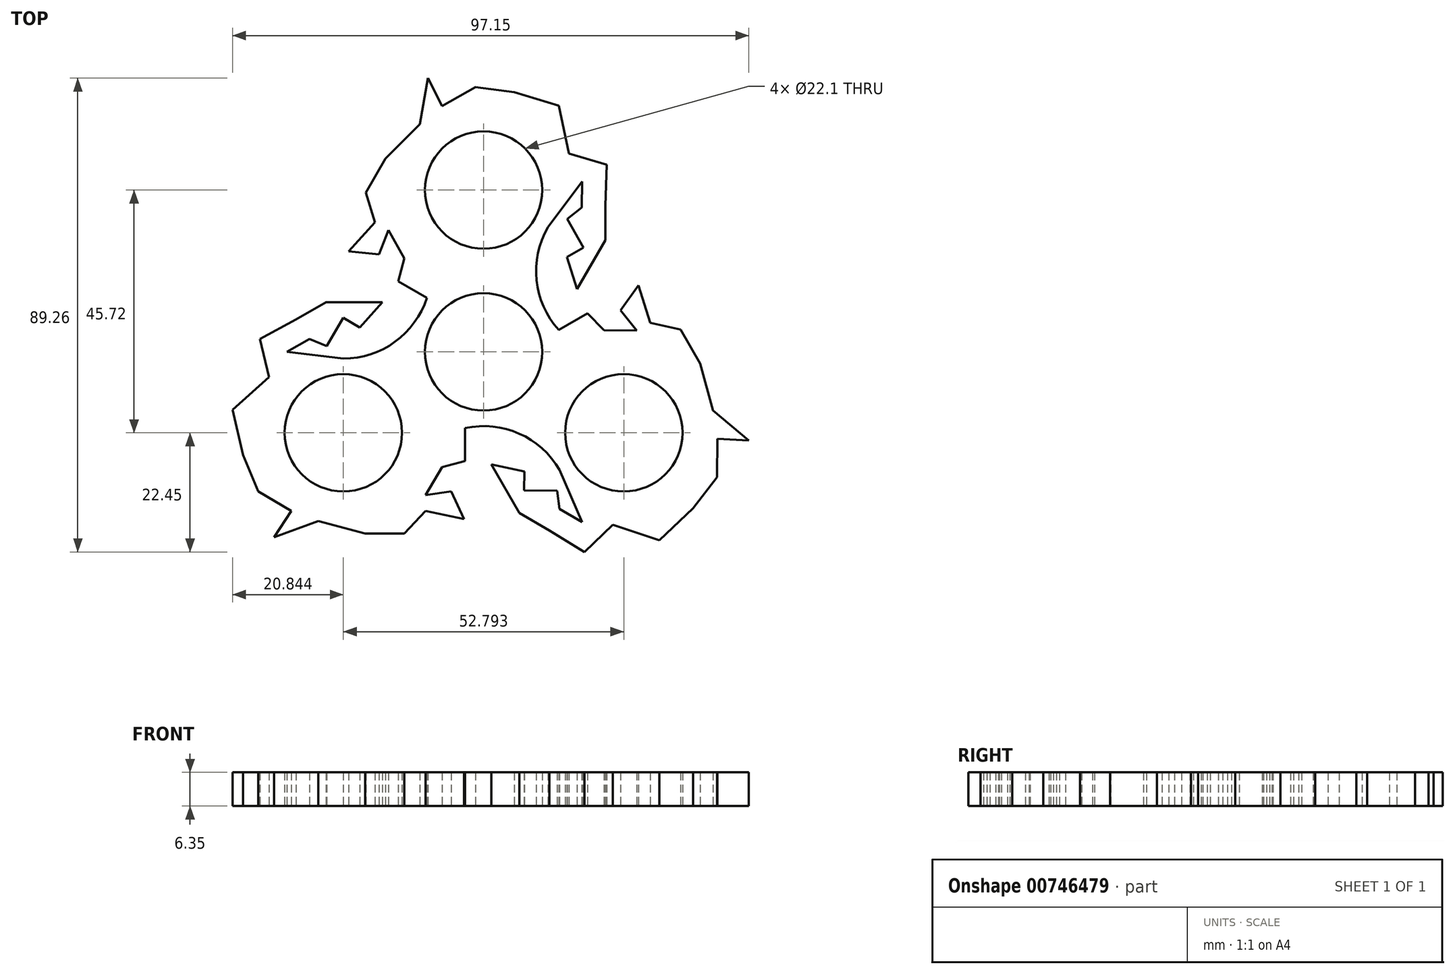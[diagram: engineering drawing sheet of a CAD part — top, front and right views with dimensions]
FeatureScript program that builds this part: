
annotation { "Feature Type Name" : "Feature", "Feature Type Description" : "" }
export const myFeature = defineFeature(function(context is Context, id is Id, definition is map)
    precondition{}
    {
        {
            var Q0;
            Q0=qCreatedBy(makeId("Top.planeOp"),FACE);
            var sketch = newSketch(context, id + "F0", { "sketchPlane" : qUnion([Q0])});
            skCircle(sketch, "E0", {"center": v(0, 0) * mm, "radius": 11.05 * mm});
            skCircle(sketch, "E1", {"center": v(0, 0) * mm, "radius": 13.97 * mm});
            skCircle(sketch, "E2", {"center": v(0, 30.48) * mm, "radius": 11.05 * mm});
            skCircle(sketch, "E3", {"center": v(0, 30.48) * mm, "radius": 13.97 * mm});
            skCircle(sketch, "E4.1.0", {"center": v(-26.4, -15.24) * mm, "radius": 13.97 * mm});
            skCircle(sketch, "E4.1.1", {"center": v(-26.4, -15.24) * mm, "radius": 11.05 * mm});
            skCircle(sketch, "E4.2.0", {"center": v(26.4, -15.24) * mm, "radius": 13.97 * mm});
            skCircle(sketch, "E4.2.1", {"center": v(26.4, -15.24) * mm, "radius": 11.05 * mm});
            skArc(sketch, "E5", {"start": v(-26.4, -1.27) * mm, "mid": v(-12.1, 6.99) * mm, "end": v(-12.1, 23.5) * mm});
            skArc(sketch, "E6.1.0", {"start": v(14.3, -22.22) * mm, "mid": v(0, -13.97) * mm, "end": v(-14.3, -22.23) * mm});
            skArc(sketch, "E6.2.0", {"start": v(12.1, 23.5) * mm, "mid": v(12.1, 6.99) * mm, "end": v(26.4, -1.27) * mm});
            skLineSegment(sketch, "E7", {"start": v(-37.03, 0) * mm, "end": v(-32.77, 2.41) * mm});
            skLineSegment(sketch, "E8", {"start": v(-32.77, 2.41) * mm, "end": v(-29.55, 1.1) * mm});
            skLineSegment(sketch, "E9", {"start": v(-29.55, 1.1) * mm, "end": v(-26.4, 6.44) * mm});
            skLineSegment(sketch, "E10", {"start": v(-26.4, 6.44) * mm, "end": v(-23.32, 4.62) * mm});
            skLineSegment(sketch, "E11", {"start": v(-23.32, 4.62) * mm, "end": v(-19.05, 9.33) * mm});
            skLineSegment(sketch, "E12", {"start": v(-19.05, 9.33) * mm, "end": v(-23.12, 9.33) * mm});
            skLineSegment(sketch, "E13", {"start": v(-23.12, 9.33) * mm, "end": v(-29.65, 9.33) * mm});
            skLineSegment(sketch, "E14", {"start": v(-29.65, 9.33) * mm, "end": v(-35.32, 6.1) * mm});
            skLineSegment(sketch, "E15", {"start": v(-35.32, 6.1) * mm, "end": v(-42.13, 2.41) * mm});
            skLineSegment(sketch, "E16", {"start": v(-42.13, 2.41) * mm, "end": v(-40.37, -4.74) * mm});
            skLineSegment(sketch, "E17", {"start": v(-40.37, -4.74) * mm, "end": v(-47.24, -10.92) * mm});
            skLineSegment(sketch, "E18", {"start": v(-47.24, -10.92) * mm, "end": v(-45.25, -19.44) * mm});
            skLineSegment(sketch, "E19", {"start": v(-45.25, -19.44) * mm, "end": v(-42.42, -26.24) * mm});
            skLineSegment(sketch, "E20", {"start": v(-42.42, -26.24) * mm, "end": v(-36.17, -29.93) * mm});
            skLineSegment(sketch, "E21", {"start": v(-36.17, -29.93) * mm, "end": v(-39.4, -34.88) * mm});
            skLineSegment(sketch, "E22", {"start": v(-39.4, -34.88) * mm, "end": v(-31.15, -31.86) * mm});
            skLineSegment(sketch, "E23", {"start": v(-31.15, -31.86) * mm, "end": v(-22.27, -34.19) * mm});
            skLineSegment(sketch, "E24", {"start": v(-22.27, -34.19) * mm, "end": v(-14.9, -34.19) * mm});
            skLineSegment(sketch, "E25", {"start": v(-14.9, -34.19) * mm, "end": v(-10.92, -29.93) * mm});
            skLineSegment(sketch, "E26", {"start": v(-10.92, -29.93) * mm, "end": v(-3.71, -31.5) * mm});
            skLineSegment(sketch, "E27", {"start": v(-3.71, -31.5) * mm, "end": v(-6.1, -26.24) * mm});
            skLineSegment(sketch, "E28", {"start": v(-6.1, -26.24) * mm, "end": v(-10.92, -26.99) * mm});
            skLineSegment(sketch, "E29", {"start": v(-10.92, -26.99) * mm, "end": v(-7.8, -21.7) * mm});
            skLineSegment(sketch, "E30", {"start": v(-7.8, -21.7) * mm, "end": v(-3.48, -20.55) * mm});
            skLineSegment(sketch, "E31", {"start": v(-3.48, -20.55) * mm, "end": v(-3.48, -13.53) * mm});
            skLineSegment(sketch, "E32", {"start": v(-37.03, 0) * mm, "end": v(-26.4, -1.27) * mm});
            skLineSegment(sketch, "E33.1.0", {"start": v(15.66, 17.88) * mm, "end": v(17.6, 11.83) * mm});
            skLineSegment(sketch, "E33.1.1", {"start": v(17.6, 11.83) * mm, "end": v(19.64, 15.36) * mm});
            skLineSegment(sketch, "E33.1.2", {"start": v(19.64, 15.36) * mm, "end": v(22.9, 21.01) * mm});
            skLineSegment(sketch, "E33.1.3", {"start": v(22.9, 21.01) * mm, "end": v(22.94, 27.54) * mm});
            skLineSegment(sketch, "E33.1.4", {"start": v(22.94, 27.54) * mm, "end": v(23.16, 35.28) * mm});
            skLineSegment(sketch, "E33.1.5", {"start": v(23.16, 35.28) * mm, "end": v(16.08, 37.33) * mm});
            skLineSegment(sketch, "E33.1.6", {"start": v(16.08, 37.33) * mm, "end": v(14.16, 46.37) * mm});
            skLineSegment(sketch, "E33.1.7", {"start": v(14.16, 46.37) * mm, "end": v(5.8, 48.9) * mm});
            skLineSegment(sketch, "E33.1.8", {"start": v(5.8, 48.9) * mm, "end": v(-1.52, 49.86) * mm});
            skLineSegment(sketch, "E33.1.9", {"start": v(-1.52, 49.86) * mm, "end": v(-7.84, 46.3) * mm});
            skLineSegment(sketch, "E33.1.10", {"start": v(-7.84, 46.3) * mm, "end": v(-10.5, 51.57) * mm});
            skLineSegment(sketch, "E33.1.11", {"start": v(-10.5, 51.57) * mm, "end": v(-12.02, 42.9) * mm});
            skLineSegment(sketch, "E33.1.12", {"start": v(-12.02, 42.9) * mm, "end": v(-18.47, 36.38) * mm});
            skLineSegment(sketch, "E33.1.13", {"start": v(-18.47, 36.38) * mm, "end": v(-22.16, 30) * mm});
            skLineSegment(sketch, "E33.1.14", {"start": v(-22.16, 30) * mm, "end": v(-20.46, 24.43) * mm});
            skLineSegment(sketch, "E33.1.15", {"start": v(-20.46, 24.43) * mm, "end": v(-25.43, 18.97) * mm});
            skLineSegment(sketch, "E33.1.16", {"start": v(-17.91, 22.95) * mm, "end": v(-14.9, 17.6) * mm});
            skLineSegment(sketch, "E33.1.17", {"start": v(-14.9, 17.6) * mm, "end": v(-16.06, 13.28) * mm});
            skLineSegment(sketch, "E33.1.18", {"start": v(-16.06, 13.28) * mm, "end": v(-9.98, 9.78) * mm});
            skLineSegment(sketch, "E33.1.19", {"start": v(15.74, 25.04) * mm, "end": v(18.78, 19.64) * mm});
            skLineSegment(sketch, "E33.1.20", {"start": v(18.47, 27.17) * mm, "end": v(15.74, 25.04) * mm});
            skLineSegment(sketch, "E33.1.21", {"start": v(18.51, 32.07) * mm, "end": v(18.47, 27.17) * mm});
            skLineSegment(sketch, "E33.1.22", {"start": v(18.51, 32.07) * mm, "end": v(12.1, 23.5) * mm});
            skLineSegment(sketch, "E33.1.23", {"start": v(-19.68, 18.4) * mm, "end": v(-17.91, 22.95) * mm});
            skLineSegment(sketch, "E33.1.24", {"start": v(-25.43, 18.97) * mm, "end": v(-19.68, 18.4) * mm});
            skLineSegment(sketch, "E33.2.0", {"start": v(7.66, -22.5) * mm, "end": v(1.44, -21.16) * mm});
            skLineSegment(sketch, "E33.2.1", {"start": v(1.44, -21.16) * mm, "end": v(3.48, -24.7) * mm});
            skLineSegment(sketch, "E33.2.2", {"start": v(3.48, -24.7) * mm, "end": v(6.74, -30.34) * mm});
            skLineSegment(sketch, "E33.2.3", {"start": v(6.74, -30.34) * mm, "end": v(12.38, -33.64) * mm});
            skLineSegment(sketch, "E33.2.4", {"start": v(12.38, -33.64) * mm, "end": v(18.98, -37.7) * mm});
            skLineSegment(sketch, "E33.2.5", {"start": v(18.98, -37.7) * mm, "end": v(24.3, -32.59) * mm});
            skLineSegment(sketch, "E33.2.6", {"start": v(24.3, -32.59) * mm, "end": v(33.08, -35.45) * mm});
            skLineSegment(sketch, "E33.2.7", {"start": v(33.08, -35.45) * mm, "end": v(39.46, -29.47) * mm});
            skLineSegment(sketch, "E33.2.8", {"start": v(39.46, -29.47) * mm, "end": v(43.94, -23.61) * mm});
            skLineSegment(sketch, "E33.2.9", {"start": v(43.94, -23.61) * mm, "end": v(44, -16.36) * mm});
            skLineSegment(sketch, "E33.2.10", {"start": v(44, -16.36) * mm, "end": v(49.91, -16.69) * mm});
            skLineSegment(sketch, "E33.2.11", {"start": v(49.91, -16.69) * mm, "end": v(43.16, -11.05) * mm});
            skLineSegment(sketch, "E33.2.12", {"start": v(43.16, -11.05) * mm, "end": v(40.74, -2.2) * mm});
            skLineSegment(sketch, "E33.2.13", {"start": v(40.74, -2.2) * mm, "end": v(37.06, 4.2) * mm});
            skLineSegment(sketch, "E33.2.14", {"start": v(37.06, 4.2) * mm, "end": v(31.38, 5.5) * mm});
            skLineSegment(sketch, "E33.2.15", {"start": v(31.38, 5.5) * mm, "end": v(29.14, 12.54) * mm});
            skLineSegment(sketch, "E33.2.16", {"start": v(28.84, 4.03) * mm, "end": v(22.7, 4.1) * mm});
            skLineSegment(sketch, "E33.2.17", {"start": v(22.7, 4.1) * mm, "end": v(19.53, 7.26) * mm});
            skLineSegment(sketch, "E33.2.18", {"start": v(19.53, 7.26) * mm, "end": v(13.46, 3.75) * mm});
            skLineSegment(sketch, "E33.2.19", {"start": v(13.82, -26.15) * mm, "end": v(7.62, -26.08) * mm});
            skLineSegment(sketch, "E33.2.20", {"start": v(14.3, -29.59) * mm, "end": v(13.82, -26.15) * mm});
            skLineSegment(sketch, "E33.2.21", {"start": v(18.51, -32.07) * mm, "end": v(14.3, -29.59) * mm});
            skLineSegment(sketch, "E33.2.22", {"start": v(18.51, -32.07) * mm, "end": v(14.3, -22.22) * mm});
            skLineSegment(sketch, "E33.2.23", {"start": v(25.77, 7.85) * mm, "end": v(28.84, 4.03) * mm});
            skLineSegment(sketch, "E33.2.24", {"start": v(29.14, 12.54) * mm, "end": v(25.77, 7.85) * mm});
            skLineSegment(sketch, "E33.anchor1", {"start": v(0, 0) * mm, "end": v(-23.32, 4.62) * mm, "construction": true});
            skLineSegment(sketch, "E34", {"start": v(15.66, 17.88) * mm, "end": v(18.78, 19.64) * mm});
            skLineSegment(sketch, "E35", {"start": v(7.62, -26.08) * mm, "end": v(7.66, -22.5) * mm});
            skSolve(sketch);
        }
        {
            var Q0;
            Q0 = qSketchRegion(id + "F0", true);
            extrude(context, id + "F1", {"entities" : qUnion([Q0]), "depth" : 6.35 * mm, "offsetDistance" : 25.4 * mm});
        }
    });
